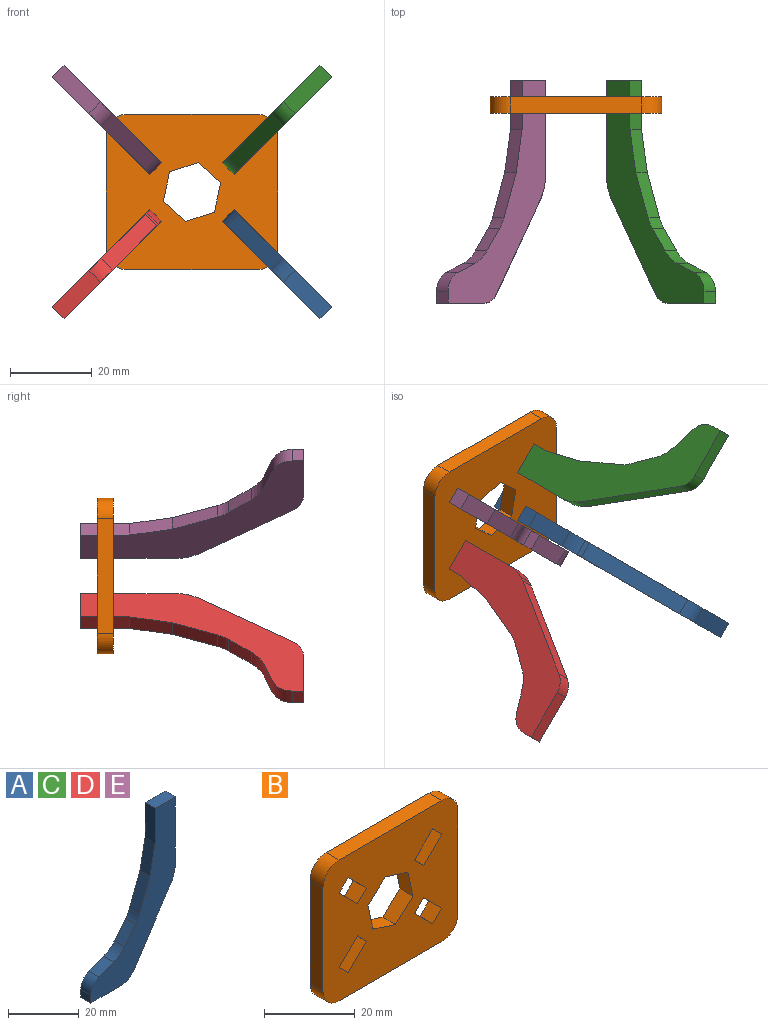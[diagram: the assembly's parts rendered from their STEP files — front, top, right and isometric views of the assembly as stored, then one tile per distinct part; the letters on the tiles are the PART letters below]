
ASSEMBLY  parts=5 mates=4
PART A: 19 faces, bbox 33.7x4x54.4 mm
  f0: plane 11.41x4mm, normal (1,0,0), area 45.7mm2, adj f1,f16,f17,f18
  f1: plane 11.99x4mm, normal (1,0,0), area 48mm2, adj f0,f2,f17,f18
  f2: plane 8x4mm, normal (0,0,1), area 32mm2, adj f1,f3,f17,f18
  f3: plane 11.99x4mm, normal (-1,0,0), area 48mm2, adj f2,f4,f17,f18
  f4: plane 10.44x4mm, normal (-0.98,0,0.19), area 42.5mm2, adj f3,f5,f17,f18
  f5: plane 11.05x4.22mm, normal (-0.93,0,0.36), area 47.3mm2, adj f4,f6,f17,f18
  f6: cylinder r=10mm len=4mm, axis (0,1,0), area 12.3mm2, adj f5,f7,f17,f18
  f7: plane 5.51x4.4mm, normal (-0.78,0,0.62), area 28.2mm2, adj f6,f8,f17,f18
  f8: cylinder r=10mm len=4.32mm, axis (0,1,0), area 21.6mm2, adj f7,f9,f17,f18
  f9: plane 5.89x4mm, normal (-0.35,0,0.94), area 25.1mm2, adj f8,f10,f17,f18
  f10: cylinder r=5mm len=4.68mm, axis (0,1,0), area 24.3mm2, adj f9,f11,f17,f18
  f11: plane 4x2.72mm, normal (-1,0,0), area 10.9mm2, adj f10,f12,f17,f18
  f12: plane 12.59x4mm, normal (0,0,-1), area 50.4mm2, adj f11,f13,f17,f18
  f13: cylinder r=5mm len=4.18mm, axis (0,1,0), area 19.8mm2, adj f12,f14,f17,f18
  f14: plane 23.22x15.24mm, normal (0.84,0,-0.55), area 111.1mm2, adj f13,f15,f17,f18
  f15: plane 4x0.98mm, normal (0.87,0,-0.5), area 4.5mm2, adj f14,f16,f17,f18
  f16: cylinder r=10mm len=4.55mm, axis (0,1,0), area 18.9mm2, adj f0,f15,f17,f18
  f17: plane 54.41x33.65mm, normal (0,-1,0), area 579.1mm2, adj f0,f1,f2,f3,f4,f5,f6,f7
  f18: plane 54.41x33.65mm, normal (0,1,0), area 579.1mm2, adj f0,f1,f2,f3,f4,f5,f6,f7
PART B: 32 faces, bbox 42x4x38 mm
  f0: plane 5.66x5.66mm, normal (-0.71,0,-0.71), area 32mm2, adj f1,f29,f30,f31
  f1: plane 4x2.83mm, normal (-0.71,0,0.71), area 16mm2, adj f0,f2,f30,f31
  f2: plane 5.66x5.66mm, normal (0.71,0,0.71), area 32mm2, adj f1,f29,f30,f31
  f3: plane 28x4mm, normal (-1,0,0), area 112mm2, adj f4,f24,f30,f31
  f4: cylinder r=5mm len=5mm, axis (0,1,0), area 31.4mm2, adj f3,f5,f30,f31
  f5: plane 32x4mm, normal (0,0,-1), area 128mm2, adj f4,f6,f30,f31
  f6: cylinder r=5mm len=5mm, axis (0,1,0), area 31.4mm2, adj f5,f7,f30,f31
  f7: plane 28x4mm, normal (1,0,0), area 112mm2, adj f6,f8,f30,f31
  f8: cylinder r=5mm len=5mm, axis (0,1,0), area 31.4mm2, adj f7,f9,f30,f31
  f9: plane 32x4mm, normal (0,0,1), area 128mm2, adj f8,f24,f30,f31
  f10: plane 4x2.83mm, normal (-0.71,0,0.71), area 16mm2, adj f11,f25,f30,f31
  f11: plane 5.66x5.66mm, normal (0.71,0,0.71), area 32mm2, adj f10,f12,f30,f31
  f12: plane 4x2.83mm, normal (0.71,0,-0.71), area 16mm2, adj f11,f25,f30,f31
  f13: plane 4x2.83mm, normal (0.71,0,0.71), area 16mm2, adj f14,f26,f30,f31
  f14: plane 5.66x5.66mm, normal (0.71,0,-0.71), area 32mm2, adj f13,f15,f30,f31
  f15: plane 4x2.83mm, normal (-0.71,0,-0.71), area 16mm2, adj f14,f26,f30,f31
  f16: plane 5.66x5.66mm, normal (0.71,0,-0.71), area 32mm2, adj f17,f27,f30,f31
  f17: plane 4x2.83mm, normal (-0.71,0,-0.71), area 16mm2, adj f16,f18,f30,f31
  f18: plane 5.66x5.66mm, normal (-0.71,0,0.71), area 32mm2, adj f17,f27,f30,f31
  f19: plane 7.2x4mm, normal (-0.98,0,-0.21), area 29.4mm2, adj f20,f28,f30,f31
  f20: plane 5.47x4.93mm, normal (-0.67,0,0.74), area 29.4mm2, adj f19,f21,f30,f31
  f21: plane 7x4mm, normal (0.31,0,0.95), area 29.4mm2, adj f20,f22,f30,f31
  f22: plane 7.2x4mm, normal (0.98,0,0.21), area 29.4mm2, adj f21,f23,f30,f31
  f23: plane 5.47x4.93mm, normal (0.67,0,-0.74), area 29.4mm2, adj f22,f28,f30,f31
  f24: cylinder r=5mm len=5mm, axis (0,1,0), area 31.4mm2, adj f3,f9,f30,f31
  f25: plane 5.66x5.66mm, normal (-0.71,0,-0.71), area 32mm2, adj f10,f12,f30,f31
  f26: plane 5.66x5.66mm, normal (-0.71,0,0.71), area 32mm2, adj f13,f15,f30,f31
  f27: plane 4x2.83mm, normal (0.71,0,0.71), area 16mm2, adj f16,f18,f30,f31
  f28: plane 7x4mm, normal (-0.31,0,-0.95), area 29.4mm2, adj f19,f23,f30,f31
  f29: plane 4x2.83mm, normal (0.71,0,-0.71), area 16mm2, adj f0,f2,f30,f31
  f30: plane 42x38mm, normal (0,-1,0), area 1305.8mm2, adj f0,f1,f2,f3,f4,f5,f6,f7
  f31: plane 42x38mm, normal (0,1,0), area 1305.8mm2, adj f0,f1,f2,f3,f4,f5,f6,f7
PART C: same geometry as A
PART D: same geometry as A
PART E: same geometry as A
PLACE A rot(axis=(-0.28,-0.68,-0.68),148.6deg) t=(-52.95,-27.38,115.65)mm
PLACE B rot(axis=(0,0,1),180deg) t=(-127.07,22.45,79.89)mm fixed
PLACE C rot(axis=(-0.28,0.68,0.68),148.6deg) t=(-55.78,-27.38,136.89)mm
PLACE D rot(axis=(-0.86,-0.36,-0.36),98.4deg) t=(-80.53,-27.38,112.82)mm
PLACE E rot(axis=(-0.86,0.36,0.36),98.4deg) t=(-83.36,-27.38,134.06)mm
MATE fastened B.f12 <-> D.f1  axis (-0.71,0,-0.71) through (-77.08,24.45,119.1)mm
MATE fastened B.f27 <-> E.f1  axis (-0.71,0,0.71) through (-77.08,24.45,130.61)mm
MATE fastened A.f3 <-> B.f13  axis (0.71,0,-0.71) through (-53.57,24.45,113.44)mm
MATE fastened B.f29 <-> C.f3  axis (-0.71,0,-0.71) through (-53.57,24.45,136.27)mm
